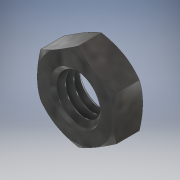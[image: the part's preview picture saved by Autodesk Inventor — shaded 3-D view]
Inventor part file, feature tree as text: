
AUTODESK INVENTOR PART (.ipt)
format: ipt  version: 2017 (Build 210142000, 142)  size: 303,104 bytes
history: native  units: mm
features: other x1, mirror x1
ambient origin geometry x8: Origin, YZ Plane, XZ Plane, XY Plane, X Axis, Y Axis, Z Axis, Center Point
bodies: Body1 (feature_tree)
feature tree (2):
  other  "Sólido1"
  mirror  "Mirror1"
